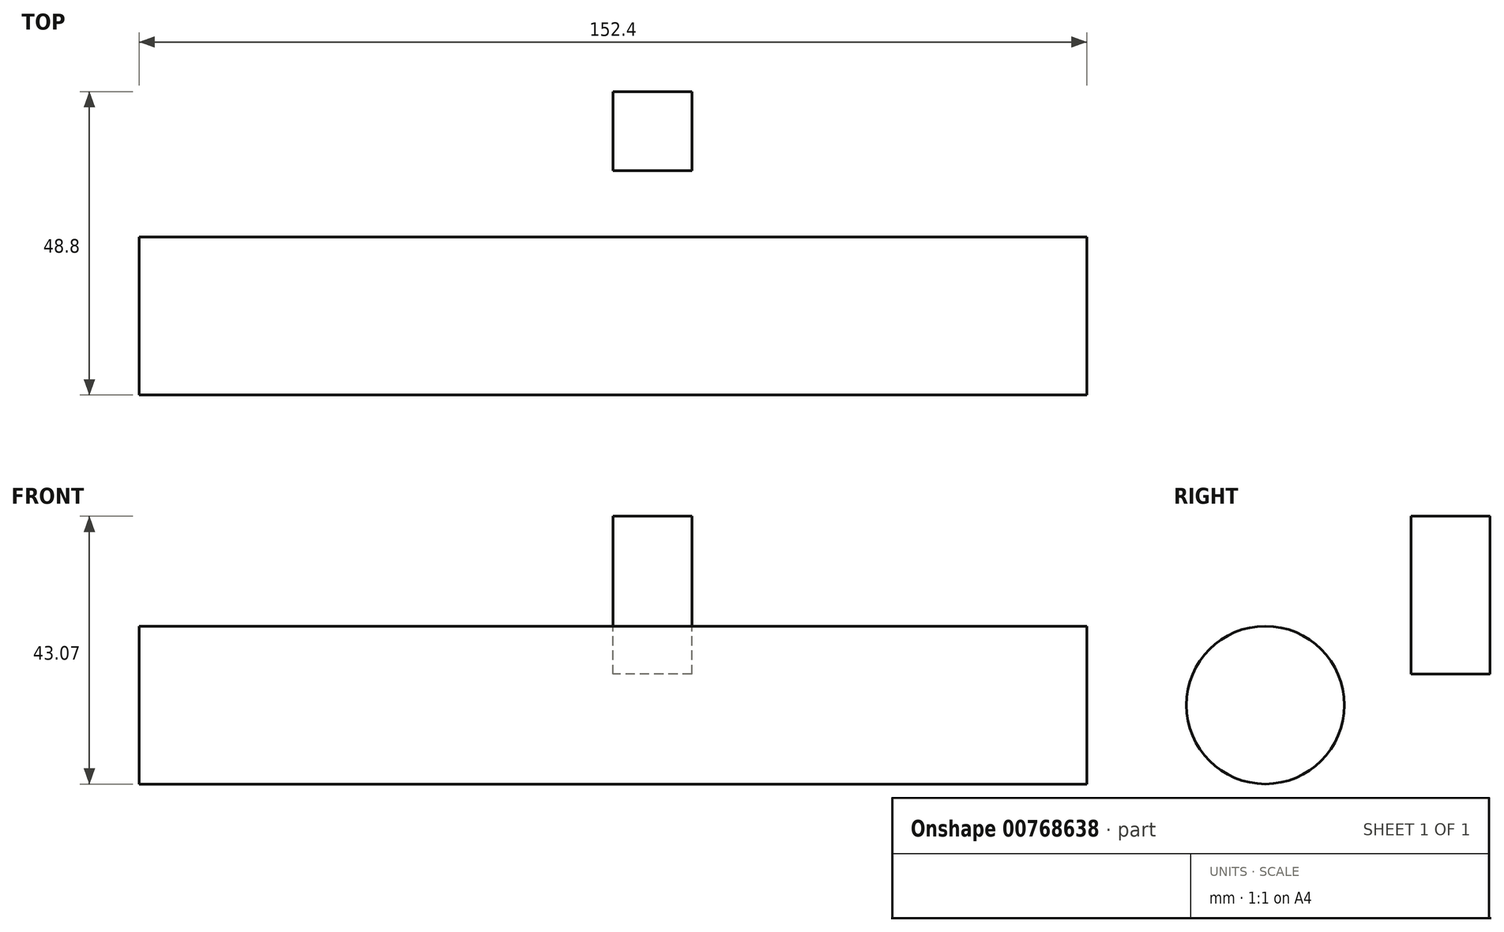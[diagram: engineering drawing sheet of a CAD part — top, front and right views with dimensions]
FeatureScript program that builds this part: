
annotation { "Feature Type Name" : "Feature", "Feature Type Description" : "" }
export const myFeature = defineFeature(function(context is Context, id is Id, definition is map)
    precondition{}
    {
        {
            var Q0;
            Q0=qCreatedBy(makeId("Right.planeOp"),FACE);
            var sketch = newSketch(context, id + "F0", { "sketchPlane" : qUnion([Q0])});
            skCircle(sketch, "E0", {"center": v(-40.99, 40.9) * mm, "radius": 12.7 * mm});
            skSolve(sketch);
        }
        {
            var Q0;
            Q0=makeQuery(id+"F0.imprint","IMPRINT",FACE,{"disambiguationData":[TD([[makeQuery(id+"F0.imprint","IMPRINT",EDGE,{"derivedFrom":sQuery(id+"F0.wireOp",EDGE,"E0")}),1.0]])]});
            extrude(context, id + "F1", {"entities" : qUnion([Q0]), "depth" : 76.2 * mm, "offsetDistance" : 25.4 * mm});
        }
        {
            var Q0;
            Q0=makeQuery(id+"F1.opExtrude","CAP_FACE",FACE,{"disambiguationData":[OSD([sQuery(id+"F0.wireOp",EDGE,"E0")])],"isStart":true});
            extrude(context, id + "F2", {"entities" : qUnion([Q0]), "operationType" : NewBodyOperationType.ADD, "depth" : 76.2 * mm, "offsetDistance" : 25.4 * mm});
        }
        {
            var Q0;
            Q0=qCreatedBy(makeId("Right.planeOp"),FACE);
            var sketch = newSketch(context, id + "F3", { "sketchPlane" : qUnion([Q0])});
            skLineSegment(sketch, "E1.bottom", {"start": v(-17.59, 45.86) * mm, "end": v(-4.89, 45.86) * mm});
            skLineSegment(sketch, "E1.top", {"start": v(-17.59, 71.26) * mm, "end": v(-4.89, 71.26) * mm});
            skLineSegment(sketch, "E1.left", {"start": v(-17.59, 45.86) * mm, "end": v(-17.59, 71.26) * mm});
            skLineSegment(sketch, "E1.right", {"start": v(-4.89, 45.86) * mm, "end": v(-4.89, 71.26) * mm});
            skSolve(sketch);
        }
        {
            var Q0;
            Q0=makeQuery(id+"F3.imprint","IMPRINT",FACE,{"disambiguationData":[TD([[makeQuery(id+"F3.imprint","IMPRINT",EDGE,{"derivedFrom":sQuery(id+"F3.wireOp",EDGE,"E1.bottom")}),1.0]])]});
            extrude(context, id + "F4", {"entities" : qUnion([Q0]), "depth" : 12.7 * mm, "offsetDistance" : 25.4 * mm});
        }
    });
